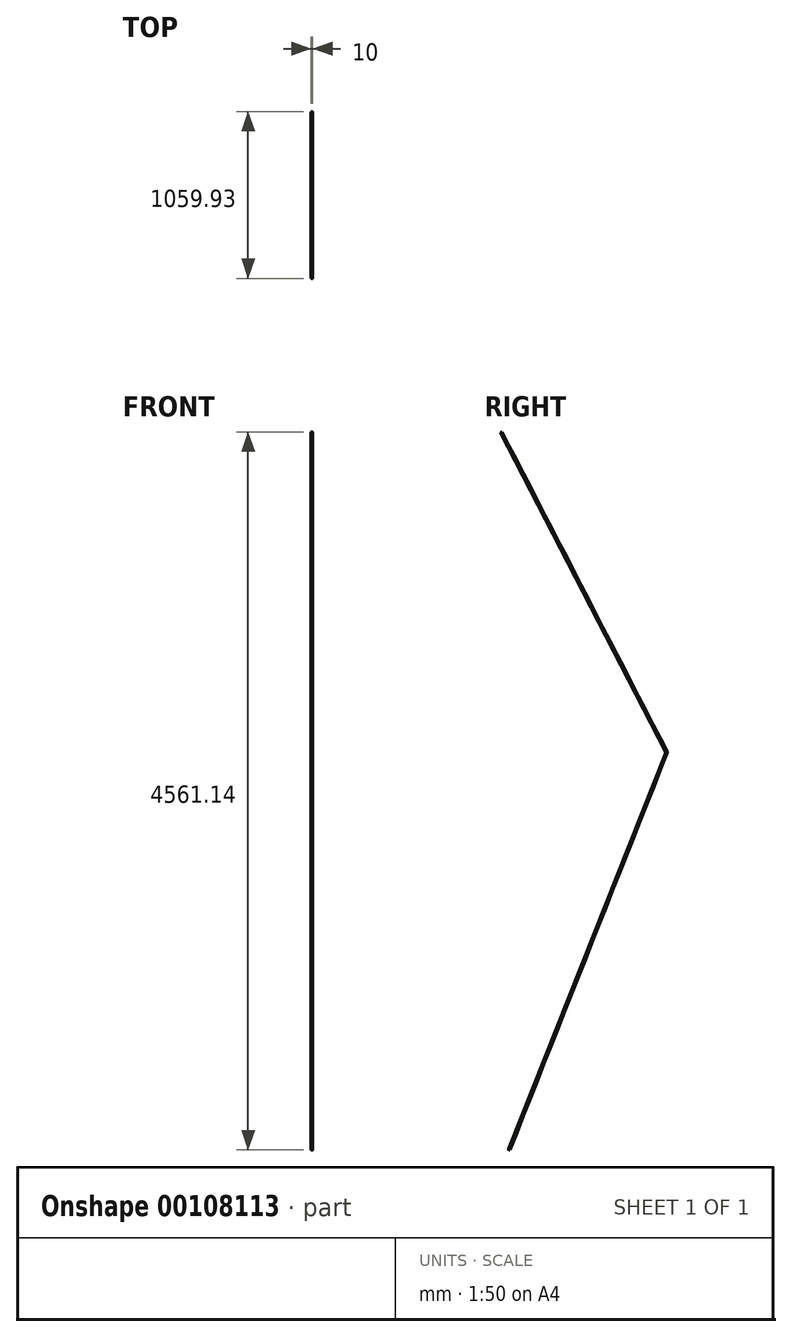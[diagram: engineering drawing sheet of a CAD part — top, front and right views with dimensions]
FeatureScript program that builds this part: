
annotation { "Feature Type Name" : "Feature", "Feature Type Description" : "" }
export const myFeature = defineFeature(function(context is Context, id is Id, definition is map)
    precondition{}
    {
        {
            assignVariable(context, id + "F0", {"name" : "Y1", "anyValue" : 0});
        }
        {
            var Q0;
            Q0=qCreatedBy(makeId("Front.planeOp"),FACE);
            cPlane(context, id + "F1", {"entities" : qUnion([Q0]), "cplaneType" : CPlaneType.OFFSET, "offset" : (getVariable(context, 'Y1')) * mm, "oppositeDirection" : true, "width" : 150 * mm, "height" : 150 * mm});
        }
        {
            var Q0;
            Q0=qCreatedBy(id+"F1.planeOp",FACE);
            var sketch = newSketch(context, id + "F2", { "sketchPlane" : qUnion([Q0])});
            skPoint(sketch, "E0", {"position": v(0, 4657) * mm});
            skSolve(sketch);
        }
        {
            assignVariable(context, id + "F3", {"name" : "Y2", "anyValue" : 1050});
        }
        {
            var Q0;
            Q0=qCreatedBy(makeId("Front.planeOp"),FACE);
            cPlane(context, id + "F4", {"entities" : qUnion([Q0]), "cplaneType" : CPlaneType.OFFSET, "offset" : (getVariable(context, 'Y2')) * mm, "oppositeDirection" : true, "width" : 150 * mm, "height" : 150 * mm});
        }
        {
            var Q0;
            Q0=qCreatedBy(id+"F4.planeOp",FACE);
            var sketch = newSketch(context, id + "F5", { "sketchPlane" : qUnion([Q0])});
            skPoint(sketch, "E1", {"position": v(0, 2625) * mm});
            skSolve(sketch);
        }
        {
            assignVariable(context, id + "F6", {"name" : "Y3", "anyValue" : 50});
        }
        {
            var Q0;
            Q0=qCreatedBy(makeId("Front.planeOp"),FACE);
            cPlane(context, id + "F7", {"entities" : qUnion([Q0]), "cplaneType" : CPlaneType.OFFSET, "offset" : (getVariable(context, 'Y3')) * mm, "oppositeDirection" : true, "width" : 150 * mm, "height" : 150 * mm});
        }
        {
            var Q0;
            Q0=qCreatedBy(id+"F7.planeOp",FACE);
            var sketch = newSketch(context, id + "F8", { "sketchPlane" : qUnion([Q0])});
            skPoint(sketch, "E2", {"position": v(0, 100) * mm});
            skSolve(sketch);
        }
        {
            var Q0;
            Q0=sQuery(id+"F5.wireOp",VERTEX,"E1");
            var Q1;
            Q1=sQuery(id+"F8.wireOp",VERTEX,"E2");
            var Q2;
            Q2=sQuery(id+"F2.wireOp",VERTEX,"E0");
            cPlane(context, id + "F9", {"entities" : qUnion([Q0, Q1, Q2]), "cplaneType" : CPlaneType.THREE_POINT, "offset" : 25 * mm, "width" : 150 * mm, "height" : 150 * mm});
        }
        {
            var Q0;
            Q0=qCreatedBy(id+"F9.planeOp",FACE);
            var sketch = newSketch(context, id + "F10", { "sketchPlane" : qUnion([Q0])});
            skPoint(sketch, "E3.0", {"position": v(0, 4657) * mm});
            skPoint(sketch, "E4.0", {"position": v(1050, 2625) * mm});
            skLineSegment(sketch, "E5", {"start": v(0, 4657) * mm, "end": v(1050, 2625) * mm});
            skPoint(sketch, "E6.0", {"position": v(50, 100) * mm});
            skLineSegment(sketch, "E7", {"start": v(1050, 2625) * mm, "end": v(50, 100) * mm});
            skSolve(sketch);
        }
        {
            var Q0;
            Q0=sQuery(id+"F10.wireOp",VERTEX,"E3.0");
            var Q1;
            Q1=sQuery(id+"F10.wireOp",EDGE,"E5");
            cPlane(context, id + "F11", {"entities" : qUnion([Q0, Q1]), "cplaneType" : CPlaneType.LINE_POINT, "offset" : 25 * mm, "width" : 150 * mm, "height" : 150 * mm});
        }
        {
            var Q0;
            Q0=qCreatedBy(id+"F11.planeOp",FACE);
            var sketch = newSketch(context, id + "F12", { "sketchPlane" : qUnion([Q0])});
            skPoint(sketch, "E8.0", {"position": v(0, -2137.87) * mm});
            skCircle(sketch, "E9", {"center": v(0, -2137.87) * mm, "radius": 5 * mm});
            skSolve(sketch);
        }
        {
            var Q0;
            Q0=makeQuery(id+"F12.imprint","IMPRINT",FACE,{"disambiguationData":[TD([[makeQuery(id+"F12.imprint","IMPRINT",EDGE,{"derivedFrom":sQuery(id+"F12.wireOp",EDGE,"E9")}),1.0]])]});
            var Q1;
            Q1=sQuery(id+"F10.wireOp",EDGE,"E5");
            var Q2;
            Q2=sQuery(id+"F10.wireOp",EDGE,"E7");
            sweep(context, id + "F13", {"profiles" : qUnion([Q0]), "path" : qUnion([Q1, Q2])});
        }
    });
